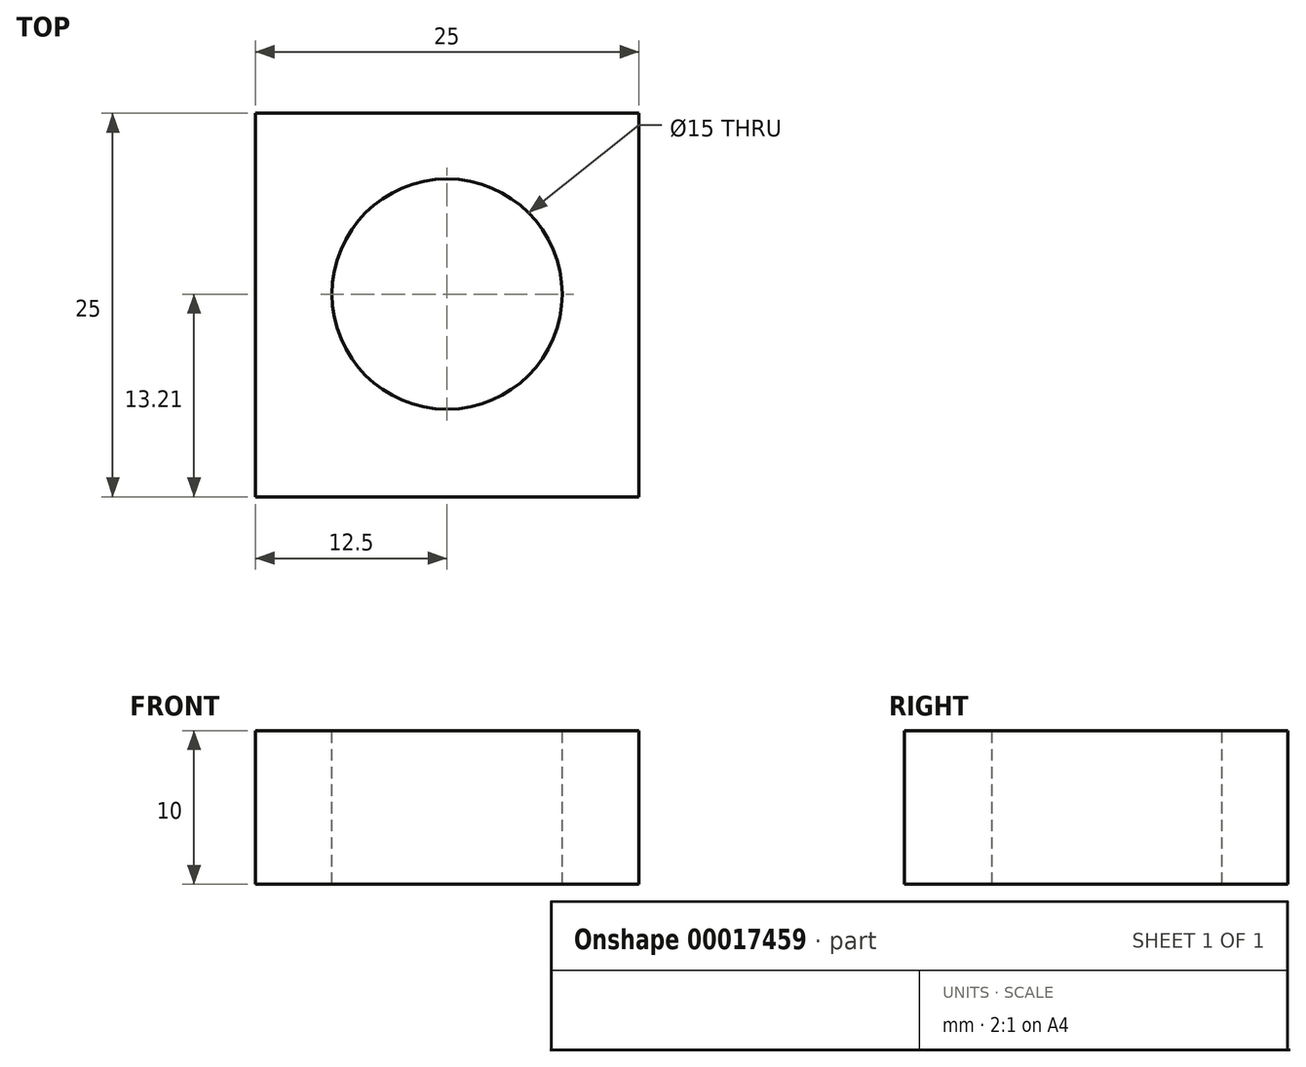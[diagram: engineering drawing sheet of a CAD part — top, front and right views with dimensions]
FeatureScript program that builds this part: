
annotation { "Feature Type Name" : "Feature", "Feature Type Description" : "" }
export const myFeature = defineFeature(function(context is Context, id is Id, definition is map)
    precondition{}
    {
        {
            var Q0;
            Q0=qCreatedBy(makeId("Top.planeOp"),FACE);
            var sketch = newSketch(context, id + "F0", { "sketchPlane" : qUnion([Q0])});
            skLineSegment(sketch, "E0.bottom", {"start": v(0, -13.21) * mm, "end": v(-25, -13.21) * mm});
            skLineSegment(sketch, "E0.top", {"start": v(0, 11.79) * mm, "end": v(-25, 11.79) * mm});
            skLineSegment(sketch, "E0.left", {"start": v(0, -13.21) * mm, "end": v(0, 11.79) * mm});
            skLineSegment(sketch, "E0.right", {"start": v(-25, -13.21) * mm, "end": v(-25, 11.79) * mm});
            skSolve(sketch);
        }
        {
            var Q0;
            Q0=makeQuery(id+"F0.imprint","IMPRINT",FACE,{"disambiguationData":[TD([[makeQuery(id+"F0.imprint","IMPRINT",EDGE,{"derivedFrom":sQuery(id+"F0.wireOp",EDGE,"E0.bottom")}),-1.0]])]});
            extrude(context, id + "F1", {"entities" : qUnion([Q0]), "depth" : 10 * mm});
        }
        {
            var Q0;
            Q0=makeQuery(id+"F1.opExtrude","CAP_FACE",FACE,{"disambiguationData":[OSD([sQuery(id+"F0.wireOp",EDGE,"E0.bottom"),sQuery(id+"F0.wireOp",EDGE,"E0.top"),sQuery(id+"F0.wireOp",EDGE,"E0.left"),sQuery(id+"F0.wireOp",EDGE,"E0.right")])],"isStart":false});
            var sketch = newSketch(context, id + "F2", { "sketchPlane" : qUnion([Q0])});
            skCircle(sketch, "E1", {"center": v(-12.5, 0) * mm, "radius": 7.5 * mm});
            skSolve(sketch);
        }
        {
            var Q0;
            Q0=makeQuery(id+"F2.imprint","IMPRINT",FACE,{"disambiguationData":[TD([[makeQuery(id+"F2.imprint","IMPRINT",EDGE,{"derivedFrom":sQuery(id+"F2.wireOp",EDGE,"E1")}),1.0]])]});
            extrude(context, id + "F3", {"entities" : qUnion([Q0]), "operationType" : NewBodyOperationType.REMOVE, "oppositeDirection" : true, "depth" : 51.34 * mm});
        }
    });
